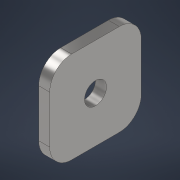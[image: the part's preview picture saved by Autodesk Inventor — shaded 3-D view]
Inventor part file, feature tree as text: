
AUTODESK INVENTOR PART (.ipt)
format: ipt  version: 2021 (Build 250183000, 183)  size: 136,192 bytes
history: native  units: mm
features: sketch x2, extrude x1, hole x1, fillet x1
ambient origin geometry x8: Origin, YZ Plane, XZ Plane, XY Plane, X Axis, Y Axis, Z Axis, Center Point
bodies: Solid1 (feature_tree)
feature tree (5):
  extrude  "Extrusion1"  Depth=50.0mm
  hole  "Hole1"  [1 undecoded]
  fillet  "Fillet2"  Radius=6.0mm
  sketch  "Sketch1"  dims[d0=50.0mm d1=50.0mm]
  sketch  "Sketch2"  dims[d2=25.0mm d3=25.0mm d4=6.0mm d5=0.0mm d6=12.0mm d7=6.0mm d8=4.0mm d9=2.0mm d10=90.0deg d11=8.0mm d12=20.594885mm d14=12.0mm]
note: 1 required parameter value undecoded (feature->parameter linkage not recoverable at this tier; creation-order binding heuristic only, values carry confidence <= 0.55)
